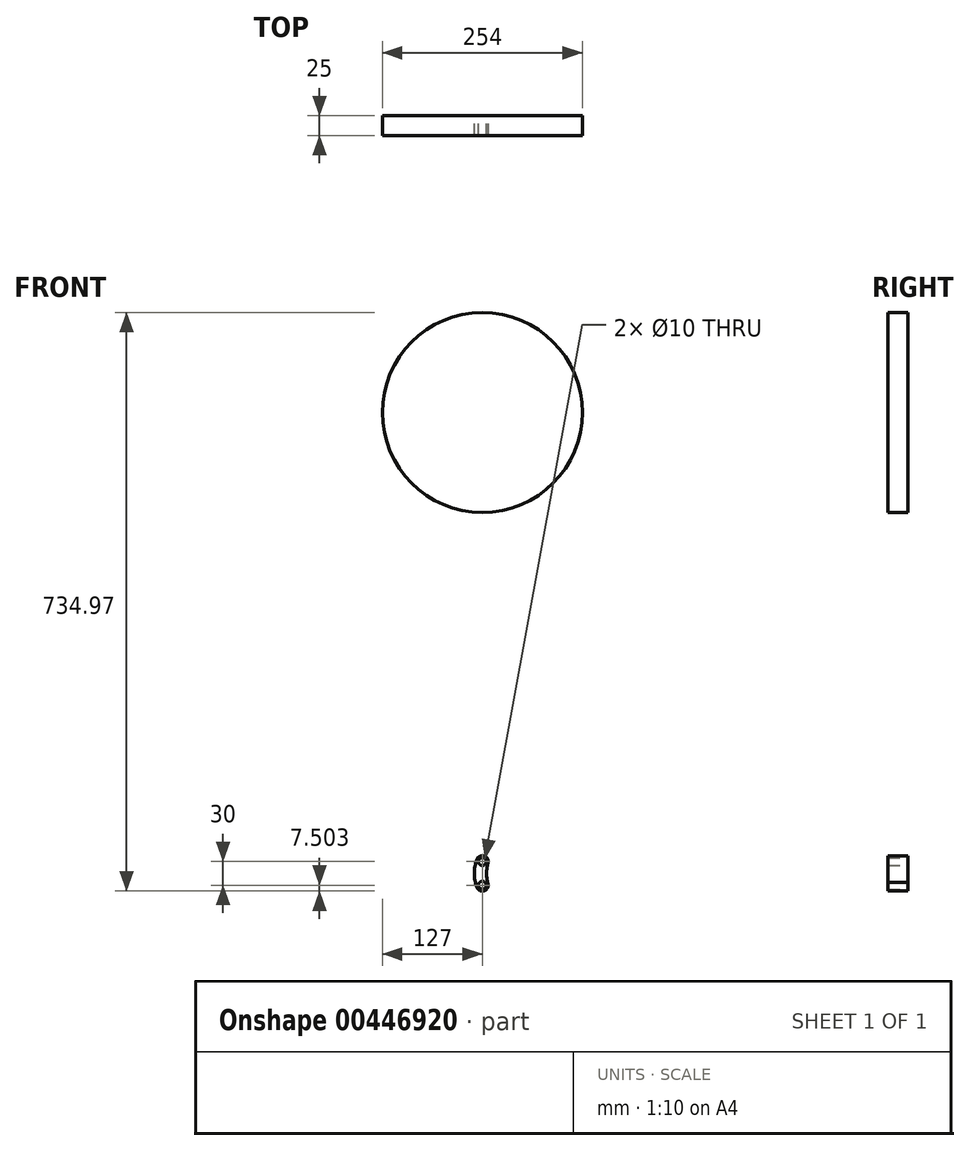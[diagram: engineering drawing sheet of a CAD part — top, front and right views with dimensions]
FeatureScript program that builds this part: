
annotation { "Feature Type Name" : "Feature", "Feature Type Description" : "" }
export const myFeature = defineFeature(function(context is Context, id is Id, definition is map)
    precondition{}
    {
        {
            var Q0;
            Q0=qCreatedBy(makeId("Front.planeOp"),FACE);
            var sketch = newSketch(context, id + "F0", { "sketchPlane" : qUnion([Q0])});
            skCircle(sketch, "E0", {"center": v(0, 587.73) * mm, "radius": 127 * mm});
            skLineSegment(sketch, "E1", {"start": v(0, 17.26) * mm, "end": v(0, -12.74) * mm, "construction": true});
            skCircle(sketch, "E2", {"center": v(0, 17.26) * mm, "radius": 5 * mm});
            skArc(sketch, "E3", {"start": v(7.23, 15.25) * mm, "mid": v(2.33, 24.4) * mm, "end": v(-7.02, 19.9) * mm});
            skCircle(sketch, "E4", {"center": v(0, -12.74) * mm, "radius": 5 * mm});
            skArc(sketch, "E5", {"start": v(-7.02, -15.38) * mm, "mid": v(3.07, -19.58) * mm, "end": v(6.65, -9.26) * mm});
            skArc(sketch, "E6", {"start": v(-7.02, 19.9) * mm, "mid": v(-10.24, 2.26) * mm, "end": v(-7.02, -15.38) * mm});
            skArc(sketch, "E7", {"start": v(7.23, 15.25) * mm, "mid": v(5.4, 1.36) * mm, "end": v(7.5, -12.49) * mm});
            skSolve(sketch);
        }
        {
            var Q0;
            Q0 = qSketchRegion(id + "F0", true);
            extrude(context, id + "F1", {"entities" : qUnion([Q0]), "endBound" : BoundingType.SYMMETRIC, "depth" : 25 * mm});
        }
    });
